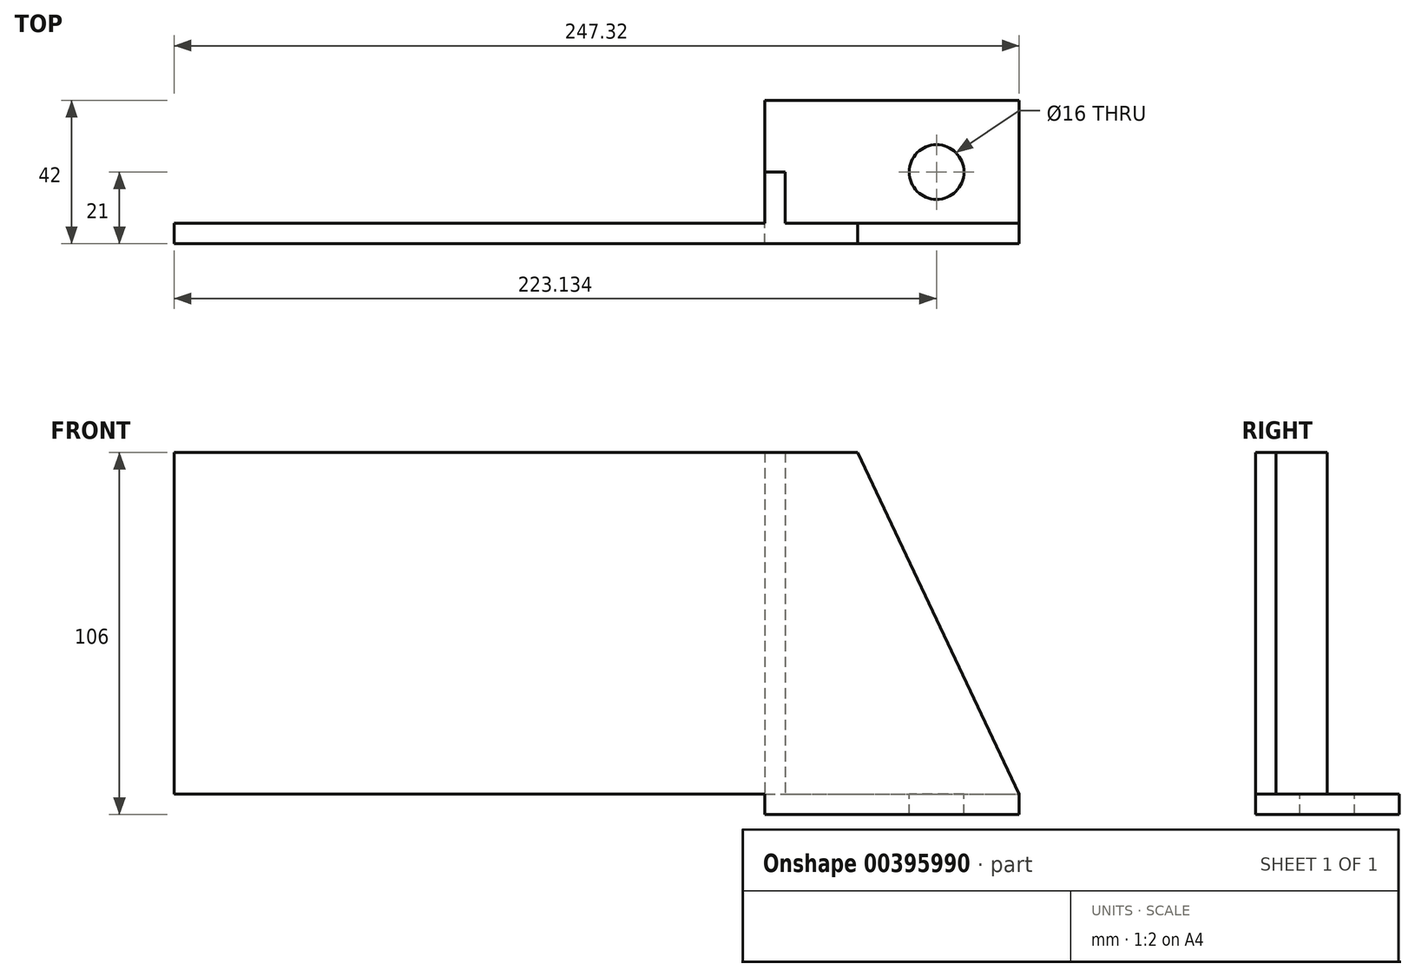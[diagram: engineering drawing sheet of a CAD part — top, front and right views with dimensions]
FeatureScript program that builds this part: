
annotation { "Feature Type Name" : "Feature", "Feature Type Description" : "" }
export const myFeature = defineFeature(function(context is Context, id is Id, definition is map)
    precondition{}
    {
        {
            var Q0;
            Q0=qCreatedBy(makeId("Front.planeOp"),FACE);
            var sketch = newSketch(context, id + "F0", { "sketchPlane" : qUnion([Q0])});
            skLineSegment(sketch, "E0.bottom", {"start": v(-200, 50) * mm, "end": v(0, 50) * mm});
            skLineSegment(sketch, "E0.top", {"start": v(-200, -50) * mm, "end": v(0, -50) * mm});
            skLineSegment(sketch, "E0.left", {"start": v(-200, 50) * mm, "end": v(-200, -50) * mm});
            skLineSegment(sketch, "E1", {"start": v(0, 50) * mm, "end": v(47.32, -50) * mm});
            skLineSegment(sketch, "E2", {"start": v(47.32, -50) * mm, "end": v(0, -50) * mm});
            skSolve(sketch);
        }
        {
            var Q0;
            Q0=makeQuery(id+"F0.imprint","IMPRINT",FACE,{"disambiguationData":[TD([[makeQuery(id+"F0.imprint","IMPRINT",EDGE,{"derivedFrom":sQuery(id+"F0.wireOp",EDGE,"E0.bottom")}),-1.0]])]});
            extrude(context, id + "F1", {"entities" : qUnion([Q0]), "depth" : 6 * mm});
        }
        {
            var Q0;
            Q0=makeQuery(id+"FREpeHqzzgq2sWv_1.boolean.opBoolean","MERGE",FACE,{"derivedFrom":[makeQuery(id+"F1.opExtrude","SWEPT_FACE",FACE,{"disambiguationData":[OSD([sQuery(id+"F0.wireOp",EDGE,"E0.top"),sQuery(id+"F0.wireOp",EDGE,"E2")])]}),makeQuery(id+"FREpeHqzzgq2sWv_1.opExtrude","SWEPT_FACE",FACE,{"disambiguationData":[OSD([sQuery(id+"F5RiXrg6He64FPH_1.wireOp",EDGE,"pJl117hb-5UdW-O4os-gsp4-0cjLAJiCC4ct.top")])]})]});
            var sketch = newSketch(context, id + "F2", { "sketchPlane" : qUnion([Q0])});
            skLineSegment(sketch, "E3.bottom", {"start": v(-27.15, 6) * mm, "end": v(47.32, 6) * mm});
            skLineSegment(sketch, "E3.top", {"start": v(-27.15, -36) * mm, "end": v(47.32, -36) * mm});
            skLineSegment(sketch, "E3.left", {"start": v(-27.15, 6) * mm, "end": v(-27.15, -36) * mm});
            skLineSegment(sketch, "E3.right", {"start": v(47.32, 6) * mm, "end": v(47.32, -36) * mm});
            skSolve(sketch);
        }
        {
            var Q0;
            {var subQ12=sQuery(id+"F2.wireOp",EDGE,"E3.bottom");Q0=makeQuery(id+"F2.imprint","IMPRINT",FACE,{"disambiguationData":[TD([[makeQuery(id+"F2.imprint","IMPRINT",EDGE,{"derivedFrom":subQ12}),-1.0]])]});}
            var Q1;
            {var subQ7=sQuery(id+"F2.wireOp",EDGE,"E3.top");Q1=makeQuery(id+"F2.imprint","IMPRINT",FACE,{"disambiguationData":[TD([[makeQuery(id+"F2.imprint","IMPRINT",EDGE,{"derivedFrom":subQ7}),1.0]])]});}
            extrude(context, id + "F3", {"entities" : qUnion([Q0, Q1]), "operationType" : NewBodyOperationType.ADD, "depth" : 6 * mm});
        }
        {
            var Q0;
            Q0=makeQuery(id+"F3.opExtrude","CAP_FACE",FACE,{"disambiguationData":[OSD([sQuery(id+"F2.wireOp",EDGE,"E3.bottom"),sQuery(id+"F2.wireOp",EDGE,"E3.top"),sQuery(id+"F2.wireOp",EDGE,"E3.left"),sQuery(id+"F2.wireOp",EDGE,"E3.right")])],"isStart":true});
            var sketch = newSketch(context, id + "F4", { "sketchPlane" : qUnion([Q0])});
            skPoint(sketch, "E4.centerSnap0", {"position": v(47.32, 18) * mm});
            skPoint(sketch, "E5", {"position": v(23.13, 15) * mm});
            skSolve(sketch);
        }
        {
            var Q0;
            Q0=sQuery(id+"F4.wireOp",VERTEX,"E5");
            var Q1;
            Q1=makeQuery(id+"F1.opExtrude","SWEPT_BODY",BODY,{"disambiguationData":[OSD([sQuery(id+"F0.wireOp",EDGE,"E0.bottom"),sQuery(id+"F0.wireOp",EDGE,"E0.top"),sQuery(id+"F0.wireOp",EDGE,"E0.left"),sQuery(id+"F0.wireOp",EDGE,"E1"),sQuery(id+"F0.wireOp",EDGE,"E2")])]});
            hole(context, id + "F5", {"style" : HoleStyle.SIMPLE, "endStyle" : HoleEndStyle.THROUGH, "holeDiameter" : 16 * mm, "isTappedThrough" : true, "tappedDepth" : 12.7 * mm, "tapClearance" : 3, "locations" : qUnion([Q0]), "scope" : qUnion([Q1])});
        }
        {
            var Q0;
            Q0=makeQuery(id+"F1.opExtrude","CAP_FACE",FACE,{"disambiguationData":[OSD([sQuery(id+"F0.wireOp",EDGE,"E0.bottom"),sQuery(id+"F0.wireOp",EDGE,"E0.top"),sQuery(id+"F0.wireOp",EDGE,"E0.left"),sQuery(id+"F0.wireOp",EDGE,"E1"),sQuery(id+"F0.wireOp",EDGE,"E2")])],"isStart":true});
            var sketch = newSketch(context, id + "F6", { "sketchPlane" : qUnion([Q0])});
            skLineSegment(sketch, "E6.bottom", {"start": v(21.15, 50) * mm, "end": v(27.15, 50) * mm});
            skLineSegment(sketch, "E6.top", {"start": v(19.7, -50) * mm, "end": v(25.7, -50) * mm});
            skLineSegment(sketch, "E6.left", {"start": v(21.15, 50) * mm, "end": v(21.15, -50) * mm});
            skLineSegment(sketch, "E6.right", {"start": v(27.15, 50) * mm, "end": v(27.15, -50) * mm});
            skSolve(sketch);
        }
        {
            var Q0;
            Q0=makeQuery(id+"F6.imprint","IMPRINT",FACE,{"disambiguationData":[TD([[makeQuery(id+"F6.imprint","IMPRINT",EDGE,{"derivedFrom":sQuery(id+"F6.wireOp",EDGE,"E6.bottom")}),1.0]])]});
            extrude(context, id + "F7", {"entities" : qUnion([Q0]), "operationType" : NewBodyOperationType.ADD, "depth" : 15 * mm});
        }
    });
